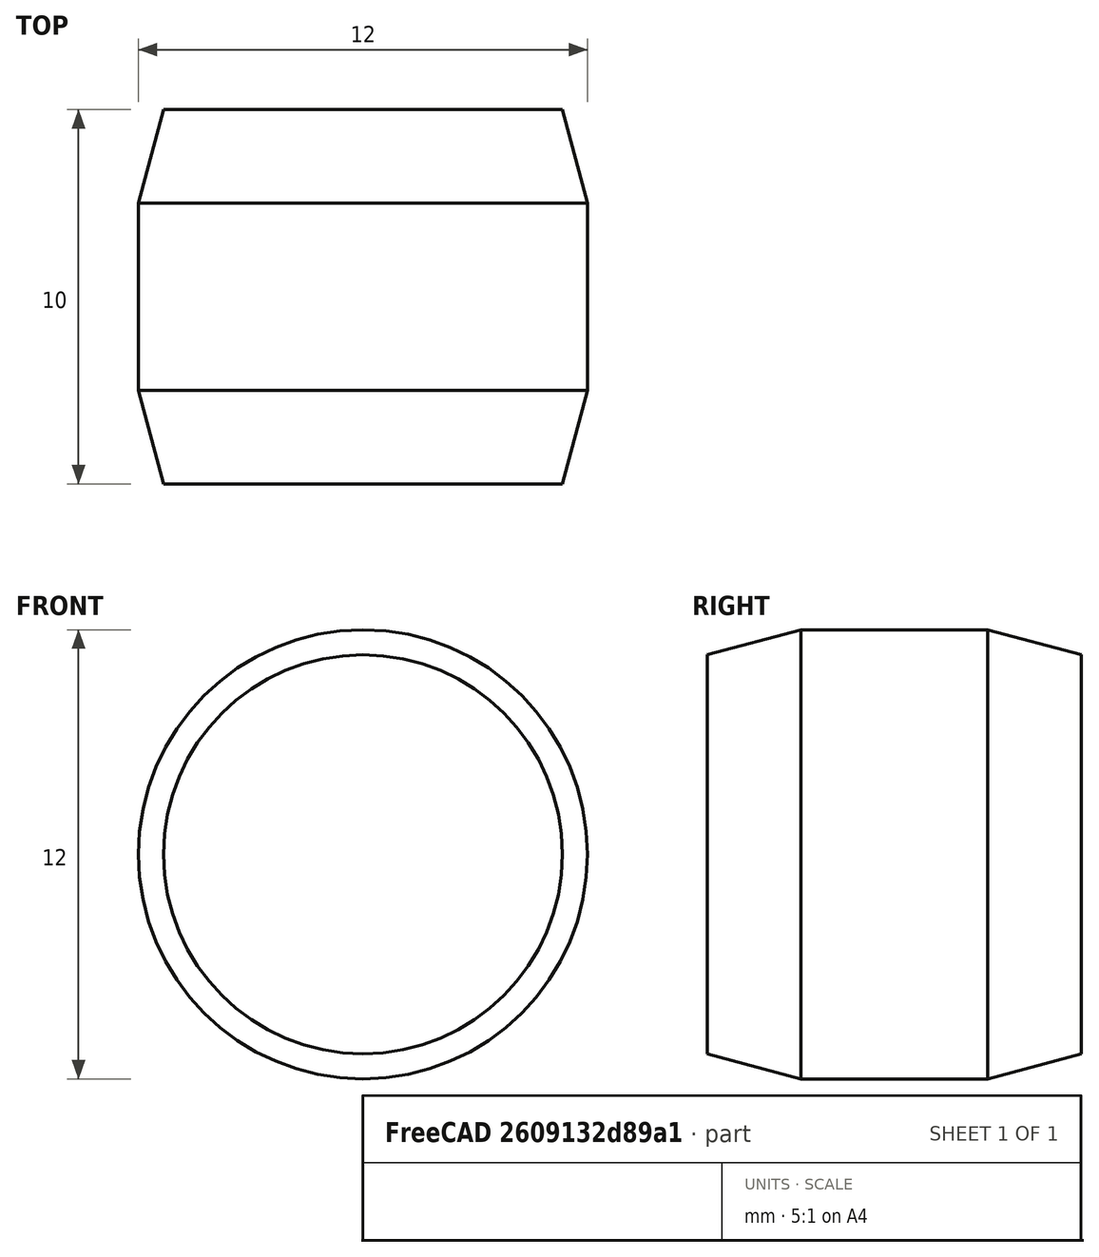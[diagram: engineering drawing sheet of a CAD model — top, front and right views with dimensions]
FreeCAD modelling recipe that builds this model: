
FCSTD DOCUMENT  (FreeCAD 0.15R4470 (Git))
Label: Zyl-Stift_ISO_2338-12x10
License: CC-BY 3.0
LicenseURL: http://creativecommons.org/licenses/by/3.0/
objects: Sketcher::SketchObject×1, PartDesign::Revolution×1
note: 3 computed .brp shape members not serialized (recipe doc carries the construction recipe); baked Part::Feature solids carry a one-line shape summary decoded from their .brp

FEATURE [Sketcher::SketchObject] Sketch
  Placement = pos=(0,0,0) rot=(0.57735,0.57735,0.57735;2.0944rad)
  sketch-geometry (7):
    g0: LineSegment StartX=0 StartY=0 StartZ=0 EndX=0 EndY=5.33013 EndZ=0
    g1: LineSegment StartX=0 StartY=5.33013 StartZ=0 EndX=2.5 EndY=6 EndZ=0
    g2: LineSegment StartX=2.5 StartY=6 StartZ=0 EndX=7.5 EndY=6 EndZ=0
    g3: LineSegment StartX=7.5 StartY=6 StartZ=0 EndX=10 EndY=5.33013 EndZ=0
    g4: LineSegment StartX=10 StartY=5.33013 StartZ=0 EndX=10 EndY=0 EndZ=0
    g5: LineSegment StartX=10 StartY=0 StartZ=0 EndX=0 EndY=0 EndZ=0
    g6: LineSegment [constr] StartX=0 StartY=5.33013 StartZ=0 EndX=10 EndY=5.33013 EndZ=0
  constraints (19):
    c: Coincident(g0,g-1)
    c: PointOnObject(g0,g-2)
    c: Coincident(g0,g1)
    c: Coincident(g1,g2)
    c: Horizontal(g2)
    c: Coincident(g2,g3)
    c: Coincident(g3,g4)
    c: Vertical(g4)
    c: Coincident(g4,g5)
    c: Coincident(g5,g-1)
    c: Horizontal(g5)
    c: Equal(g3,g1)
    c: Coincident(g6,g0)
    c: Coincident(g6,g3)
    c: Horizontal(g6)
    c: Angle(g6,g1) = 0.261799
    c: DistanceY(g-1,g1) = 6
    c: DistanceX(g5) = -10
    c: DistanceX(g1) = 2.5
FEATURE [PartDesign::Revolution] Revolution  label="Zyl-Stift ISO 2338-12x10 #"
  Angle = 360
  Axis = (0,1,0)
  Base = (0,0,0)
  Placement = pos=(0,0,0) rot=(0.57735,0.57735,0.57735;2.0944rad)
  ReferenceAxis = -> Sketch [H_Axis]
  Sketch = -> Sketch
